SOLIDWORKS PART (.sldprt)
format: sldprt  version: not decoded by parser v0  size: 390,144 bytes
history: native  units: mm
features: fillet x13, sketch x10, extrude x5, cut_extrude x5, plane x3, material x1 (+8 scaffold rows collapsed)
feature tree (45):
  scaffold x8  (default folders/planes/origin — collapsed)
  material  "Duranickel(R) 301"
  plane  "Alzado"
  plane  "Planta"
  plane  "Vista lateral"
  sketch  "Croquis1"  dims[D1=31.0mm D2=12.5mm D3=15.5mm D4=6.25mm]
  extrude  "Extruir1"  Depth=0.5mm
  fillet  "Redondeo1"  Radius=1.5mm
  sketch  "Croquis2"  dims[c1.D5=5.0mm c1.D6=5.0mm c1.D7=5.0mm c1.D8=5.0mm c1.D9=2.8mm c1.D1=16.4mm c1.D2=9.2mm c1.D3=9.0mm c1.D4=4.6mm c2.D9=5.2mm c3.D9=10.0deg c3.D10=5.2mm c4.D10=10.0deg c4.D11=9.0mm]
  extrude  "Extruir2"  Depth=5.8mm
  sketch  "Croquis3"  dims[D1=0.0mm D2=0.9mm]
  cut_extrude  "Cortar-Extruir1"  Depth=9.8mm
  fillet  "Redondeo2"  Radius=0.8mm
  fillet  "Redondeo3"  Radius=0.8mm
  sketch  "Croquis4"  dims[D1=2.4mm D2=2.4mm D3=25.3mm D4=12.65mm D5=6.25mm]
  cut_extrude  "Cortar-Extruir2"  Depth=9.8mm
  fillet  "Redondeo4"  Radius=0.8mm
  sketch  "Croquis5"  dims[D1=10.5mm]
  extrude  "Extruir3"  Depth=4.5mm
  sketch  "Croquis6"  dims[D1=1.9mm D2=2.0mm]
  cut_extrude  "Cortar-Extruir3"  Depth=36.5mm
  sketch  "Croquis7"  dims[c1.D2=2.4mm c1.D4=2.4mm c1.D1=5.7mm c2.D2=2.85mm c2.D3=5.7mm c2.D4=2.85mm]
  cut_extrude  "Cortar-Extruir4"  Depth=2.5mm
  sketch  "Croquis8"
  cut_extrude  "Cortar-Extruir5"  Depth=2.5mm
  sketch  "Croquis11"
  extrude  "Extruir5"  Depth=2.2mm
  sketch  "Croquis12"  dims[D1=0.8mm D2=1.5mm]
  extrude  "Extruir6"  Depth=5.5mm
  fillet  "Redondeo5"  Radius=0.4mm
  fillet  "Redondeo6"  Radius=0.4mm
  fillet  "Redondeo7"  Radius=0.4mm
  fillet  "Redondeo8"  Radius=0.4mm
  fillet  "Redondeo9"  Radius=0.4mm
  fillet  "Redondeo10"  Radius=0.4mm
  fillet  "Redondeo11"  Radius=0.4mm
  fillet  "Redondeo12"  Radius=0.4mm
  fillet  "Redondeo13"  Radius=0.4mm
decode coverage: 31 of 33 modeling features carry decoded parameters
note: suppression state not decoded; provenance and decode notes live in map.json
